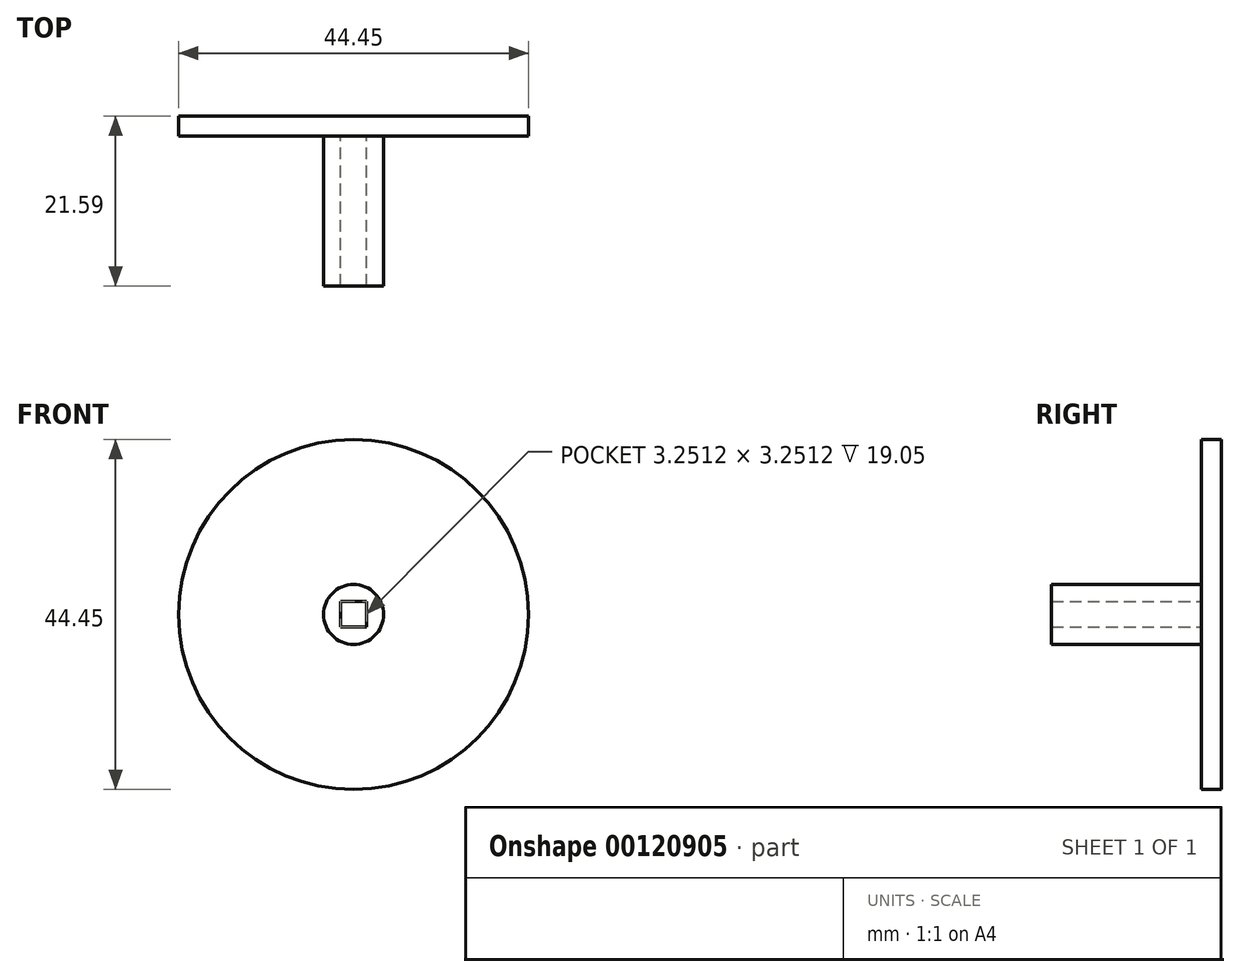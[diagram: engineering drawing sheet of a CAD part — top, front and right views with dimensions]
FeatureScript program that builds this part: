
annotation { "Feature Type Name" : "Feature", "Feature Type Description" : "" }
export const myFeature = defineFeature(function(context is Context, id is Id, definition is map)
    precondition{}
    {
        {
            var Q0;
            Q0=qCreatedBy(makeId("Front.planeOp"),FACE);
            var sketch = newSketch(context, id + "F0", { "sketchPlane" : qUnion([Q0])});
            skCircle(sketch, "E0", {"center": v(-29.83, 27.93) * mm, "radius": 22.23 * mm});
            skSolve(sketch);
        }
        {
            var Q0;
            Q0=makeQuery(id+"F0.imprint","IMPRINT",FACE,{"disambiguationData":[TD([[makeQuery(id+"F0.imprint","IMPRINT",EDGE,{"derivedFrom":sQuery(id+"F0.wireOp",EDGE,"E0")}),1.0]])]});
            extrude(context, id + "F1", {"entities" : qUnion([Q0]), "depth" : 2.54 * mm});
        }
        {
            var Q0;
            Q0=makeQuery(id+"F1.opExtrude","CAP_FACE",FACE,{"disambiguationData":[OSD([sQuery(id+"F0.wireOp",EDGE,"E0")])],"isStart":false});
            var sketch = newSketch(context, id + "F2", { "sketchPlane" : qUnion([Q0])});
            skCircle(sketch, "E1", {"center": v(-29.83, 27.93) * mm, "radius": 3.81 * mm});
            skLineSegment(sketch, "E2.bottom", {"start": v(-31.46, 29.58) * mm, "end": v(-28.2, 29.58) * mm});
            skLineSegment(sketch, "E2.top", {"start": v(-31.46, 26.33) * mm, "end": v(-28.2, 26.33) * mm});
            skLineSegment(sketch, "E2.left", {"start": v(-31.46, 29.58) * mm, "end": v(-31.46, 26.33) * mm});
            skLineSegment(sketch, "E2.right", {"start": v(-28.2, 29.58) * mm, "end": v(-28.2, 26.33) * mm});
            skLineSegment(sketch, "E3", {"start": v(-29.83, 27.93) * mm, "end": v(-28.2, 26.33) * mm, "construction": true});
            skLineSegment(sketch, "E4", {"start": v(-29.83, 27.93) * mm, "end": v(-31.46, 26.33) * mm, "construction": true});
            skSolve(sketch);
        }
        {
            var Q0;
            Q0 = qSketchRegion(id + "F2", true);
            extrude(context, id + "F3", {"entities" : qUnion([Q0]), "operationType" : NewBodyOperationType.ADD, "depth" : 19.05 * mm});
        }
    });
